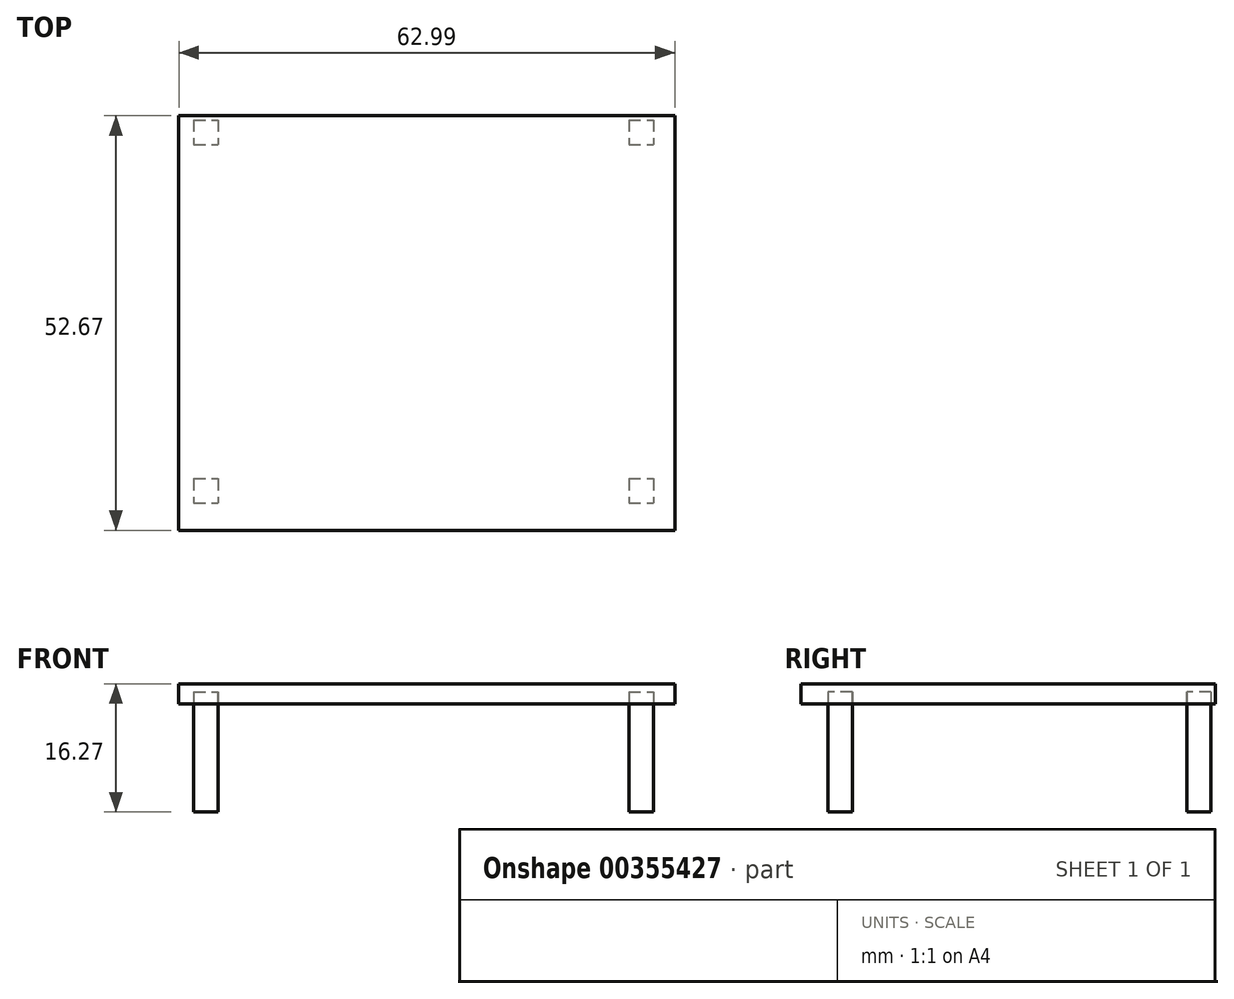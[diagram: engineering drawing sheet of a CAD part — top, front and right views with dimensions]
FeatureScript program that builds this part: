
annotation { "Feature Type Name" : "Feature", "Feature Type Description" : "" }
export const myFeature = defineFeature(function(context is Context, id is Id, definition is map)
    precondition{}
    {
        {
            var Q0;
            Q0=qCreatedBy(makeId("Top.planeOp"),FACE);
            var sketch = newSketch(context, id + "F0", { "sketchPlane" : qUnion([Q0])});
            skLineSegment(sketch, "E0.top", {"start": v(-24.98, -21.5) * mm, "end": v(27.19, -21.5) * mm});
            skLineSegment(sketch, "E0.left", {"start": v(-24.98, 20.97) * mm, "end": v(-24.98, -21.5) * mm});
            skLineSegment(sketch, "E0.right", {"start": v(27.19, 20.97) * mm, "end": v(27.19, -21.5) * mm});
            skLineSegment(sketch, "E1.bottom", {"start": v(27.19, -21.5) * mm, "end": v(30.29, -21.5) * mm});
            skLineSegment(sketch, "E1.top", {"start": v(27.19, -24.6) * mm, "end": v(30.29, -24.6) * mm});
            skLineSegment(sketch, "E1.left", {"start": v(27.19, -21.5) * mm, "end": v(27.19, -24.6) * mm});
            skLineSegment(sketch, "E1.right", {"start": v(30.29, -21.5) * mm, "end": v(30.29, -24.6) * mm});
            skLineSegment(sketch, "E2.bottom", {"start": v(-28.08, 24.07) * mm, "end": v(-24.98, 24.07) * mm});
            skLineSegment(sketch, "E2.top", {"start": v(-28.08, 20.97) * mm, "end": v(-24.98, 20.97) * mm});
            skLineSegment(sketch, "E2.left", {"start": v(-28.08, 24.07) * mm, "end": v(-28.08, 20.97) * mm});
            skLineSegment(sketch, "E2.right", {"start": v(-24.98, 24.07) * mm, "end": v(-24.98, 20.97) * mm});
            skLineSegment(sketch, "E3.bottom", {"start": v(-28.08, -21.5) * mm, "end": v(-24.98, -21.5) * mm});
            skLineSegment(sketch, "E3.top", {"start": v(-28.08, -24.6) * mm, "end": v(-24.98, -24.6) * mm});
            skLineSegment(sketch, "E3.left", {"start": v(-28.08, -21.5) * mm, "end": v(-28.08, -24.6) * mm});
            skLineSegment(sketch, "E3.right", {"start": v(-24.98, -21.5) * mm, "end": v(-24.98, -24.6) * mm});
            skLineSegment(sketch, "E4.bottom", {"start": v(27.19, 24.07) * mm, "end": v(30.29, 24.07) * mm});
            skLineSegment(sketch, "E4.top", {"start": v(27.19, 20.97) * mm, "end": v(30.29, 20.97) * mm});
            skLineSegment(sketch, "E4.left", {"start": v(27.19, 24.07) * mm, "end": v(27.19, 20.97) * mm});
            skLineSegment(sketch, "E4.right", {"start": v(30.29, 24.07) * mm, "end": v(30.29, 20.97) * mm});
            skSolve(sketch);
        }
        {
            var Q0;
            Q0=qCreatedBy(makeId("Right.planeOp"),FACE);
            var sketch = newSketch(context, id + "F1", { "sketchPlane" : qUnion([Q0])});
            skLineSegment(sketch, "E5.bottom", {"start": v(24.61, 16.27) * mm, "end": v(-28.06, 16.27) * mm});
            skLineSegment(sketch, "E5.top", {"start": v(24.61, 13.73) * mm, "end": v(-28.06, 13.73) * mm});
            skLineSegment(sketch, "E5.left", {"start": v(24.61, 16.27) * mm, "end": v(24.61, 13.73) * mm});
            skLineSegment(sketch, "E5.right", {"start": v(-28.06, 16.27) * mm, "end": v(-28.06, 13.73) * mm});
            skSolve(sketch);
        }
        {
            var Q0;
            Q0=qSketchRegion(id+"F1",true);
            extrude(context, id + "F2", {"entities" : qUnion([Q0]), "oppositeDirection" : true, "depth" : 29.97 * mm, "hasSecondDirection" : true, "secondDirectionOppositeDirection" : false, "secondDirectionDepth" : 33.02 * mm});
        }
        {
            var Q0;
            Q0=qSketchRegion(id+"F0",true);
            extrude(context, id + "F3", {"entities" : qUnion([Q0]), "depth" : 15.24 * mm});
        }
    });
